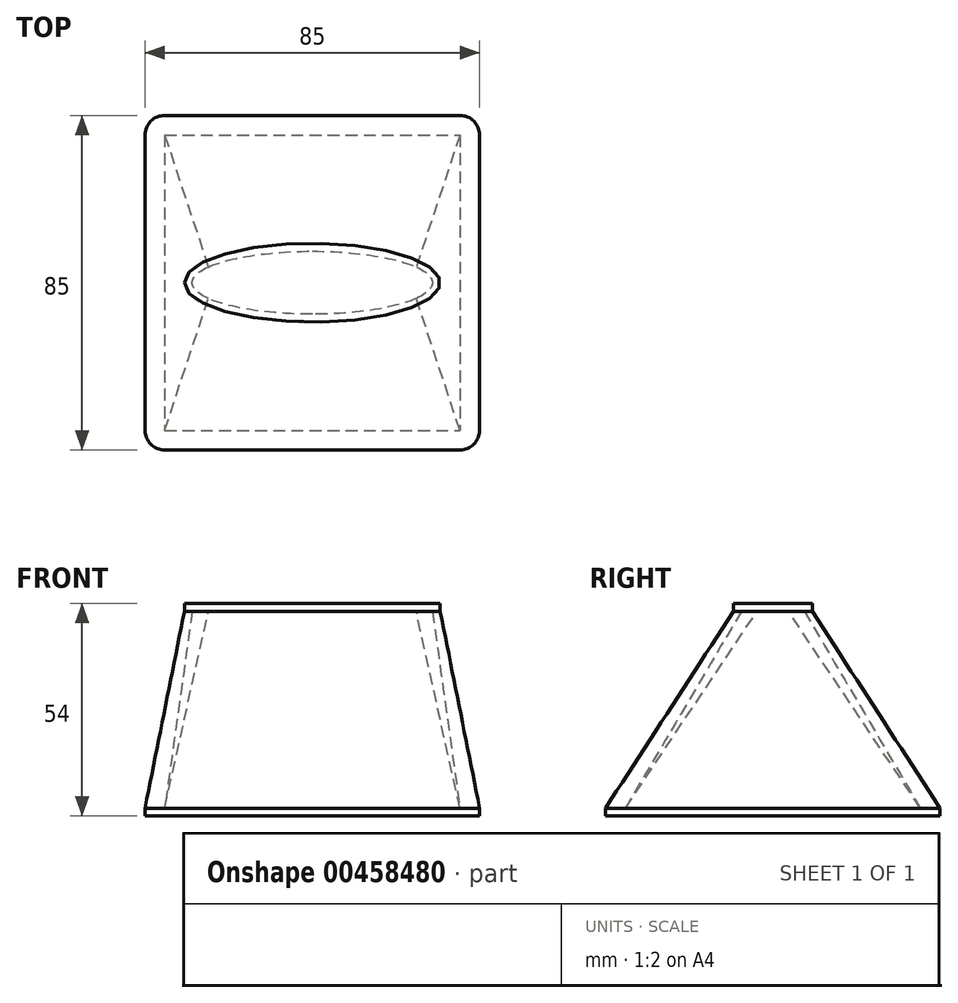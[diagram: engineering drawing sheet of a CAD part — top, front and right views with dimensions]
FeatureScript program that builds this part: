
annotation { "Feature Type Name" : "Feature", "Feature Type Description" : "" }
export const myFeature = defineFeature(function(context is Context, id is Id, definition is map)
    precondition{}
    {
        {
            var Q0;
            Q0=qCreatedBy(makeId("Top.planeOp"),FACE);
            var sketch = newSketch(context, id + "F0", { "sketchPlane" : qUnion([Q0])});
            skEllipse(sketch, "E0", {"center": v(0, 0) * mm, "majorRadius": 32.5 * mm, "minorRadius": 10 * mm, "majorAxis": v(-1, 0)});
            skSolve(sketch);
        }
        {
            var Q0;
            Q0=makeQuery(id+"F0.imprint","IMPRINT",FACE,{"disambiguationData":[TD([[makeQuery(id+"F0.imprint","IMPRINT",EDGE,{"derivedFrom":sQuery(id+"F0.wireOp",EDGE,"E0")}),1.0]])]});
            var Q1;
            Q1=sQuery(id+"F0.wireOp",EDGE,"E0");
            extrude(context, id + "F1", {"entities" : qUnion([Q0]), "surfaceEntities" : qUnion([Q1]), "depth" : 2 * mm});
        }
        {
            var Q0;
            Q0=makeQuery(id+"F1.opExtrude","SWEPT_BODY",BODY,{"disambiguationData":[OSD([sQuery(id+"F0.wireOp",EDGE,"E0")])]});
            transform(context, id + "F2", {"entities" : qUnion([Q0]), "transformType" : TransformType.TRANSLATION_3D, "dx" : 0 * mm, "dy" : 0 * mm, "dz" : 25 * mm, "makeCopy" : false});
        }
        {
            var Q0;
            Q0=qCreatedBy(makeId("Top.planeOp"),FACE);
            var sketch = newSketch(context, id + "F3", { "sketchPlane" : qUnion([Q0])});
            skLineSegment(sketch, "E1.bottom", {"start": v(-42.5, 42.5) * mm, "end": v(42.5, 42.5) * mm});
            skLineSegment(sketch, "E1.top", {"start": v(-42.5, -42.5) * mm, "end": v(42.5, -42.5) * mm});
            skLineSegment(sketch, "E1.left", {"start": v(-42.5, 42.5) * mm, "end": v(-42.5, -42.5) * mm});
            skLineSegment(sketch, "E1.right", {"start": v(42.5, 42.5) * mm, "end": v(42.5, -42.5) * mm});
            skLineSegment(sketch, "E2", {"start": v(0, -42.5) * mm, "end": v(0, 42.5) * mm, "construction": true});
            skSolve(sketch);
        }
        {
            var Q0;
            Q0 = qSketchRegion(id + "F3", true);
            extrude(context, id + "F4", {"entities" : qUnion([Q0]), "oppositeDirection" : true, "depth" : 2 * mm});
        }
        {
            var Q0;
            Q0=makeQuery(id+"F4.opExtrude","SWEPT_BODY",BODY,{"disambiguationData":[OSD([sQuery(id+"F3.wireOp",EDGE,"E1.bottom"),sQuery(id+"F3.wireOp",EDGE,"E1.top"),sQuery(id+"F3.wireOp",EDGE,"E1.left"),sQuery(id+"F3.wireOp",EDGE,"E1.right")])]});
            transform(context, id + "F5", {"entities" : qUnion([Q0]), "transformType" : TransformType.TRANSLATION_3D, "dx" : 0 * mm, "dy" : 0 * mm, "dz" : -25 * mm, "makeCopy" : false});
        }
        {
            var Q0;
            Q0=makeQuery(id+"Fj7gzEkDTdT3czc_2.opLoft","SWEPT_EDGE",EDGE,{"disambiguationData":[OSD([sQuery(id+"F0.wireOp",EDGE,"E0"),sQuery(id+"F3.wireOp",EDGE,"E1.bottom"),sQuery(id+"F3.wireOp",EDGE,"E1.left"),sQuery(id+"FQOJDwY7TzD2iMy_2.wireOp",EDGE,"0ff71cc1-0b0f-46e7-a495-bf6d35687e3b")])]});
            var Q1;
            Q1=makeQuery(id+"Fj7gzEkDTdT3czc_2.opLoft","SWEPT_EDGE",EDGE,{"disambiguationData":[OSD([sQuery(id+"F0.wireOp",EDGE,"E0"),sQuery(id+"F3.wireOp",EDGE,"E1.bottom"),sQuery(id+"F3.wireOp",EDGE,"E1.right"),sQuery(id+"FvGfQPQfCit8S9d_2.wireOp",EDGE,"579d9dbb-9344-4774-a39f-a0f3231496a0")])]});
            var Q2;
            Q2=makeQuery(id+"Fj7gzEkDTdT3czc_2.opLoft","SWEPT_EDGE",EDGE,{"disambiguationData":[OSD([sQuery(id+"F0.wireOp",EDGE,"E0"),sQuery(id+"F3.wireOp",EDGE,"E1.top"),sQuery(id+"F3.wireOp",EDGE,"E1.right"),sQuery(id+"FQOJDwY7TzD2iMy_2.wireOp",EDGE,"b4c446bf-a4a6-4e09-b549-f1406689d661")])]});
            var Q3;
            Q3=makeQuery(id+"Fj7gzEkDTdT3czc_2.opLoft","SWEPT_EDGE",EDGE,{"disambiguationData":[OSD([sQuery(id+"F0.wireOp",EDGE,"E0"),sQuery(id+"F3.wireOp",EDGE,"E1.top"),sQuery(id+"F3.wireOp",EDGE,"E1.left"),sQuery(id+"FvGfQPQfCit8S9d_2.wireOp",EDGE,"67149b96-056e-4209-8843-8e4786fcf0c8")])]});
            var Q4;
            Q4=makeQuery(id+"F4.opExtrude","SWEPT_EDGE",EDGE,{"disambiguationData":[OSD([sQuery(id+"F3.wireOp",EDGE,"E1.bottom"),sQuery(id+"F3.wireOp",EDGE,"E1.left")])]});
            var Q5;
            Q5=makeQuery(id+"F4.opExtrude","SWEPT_EDGE",EDGE,{"disambiguationData":[OSD([sQuery(id+"F3.wireOp",EDGE,"E1.bottom"),sQuery(id+"F3.wireOp",EDGE,"E1.right")])]});
            var Q6;
            Q6=makeQuery(id+"F4.opExtrude","SWEPT_EDGE",EDGE,{"disambiguationData":[OSD([sQuery(id+"F3.wireOp",EDGE,"E1.top"),sQuery(id+"F3.wireOp",EDGE,"E1.right")])]});
            var Q7;
            Q7=makeQuery(id+"F4.opExtrude","SWEPT_EDGE",EDGE,{"disambiguationData":[OSD([sQuery(id+"F3.wireOp",EDGE,"E1.top"),sQuery(id+"F3.wireOp",EDGE,"E1.left")])]});
            fillet(context, id + "F6", {"entities" : qUnion([Q0, Q1, Q2, Q3, Q4, Q5, Q6, Q7]), "radius" : 5 * mm, "tangentPropagation" : true, "allowEdgeOverflow" : false});
        }
        {
            var Q0;
            Q0=makeQuery(id+"F1.opExtrude","CAP_FACE",FACE,{"disambiguationData":[OSD([sQuery(id+"F0.wireOp",EDGE,"E0")])],"isStart":true});
            var sketch = newSketch(context, id + "F7", { "sketchPlane" : qUnion([Q0])});
            skEllipse(sketch, "E3", {"center": v(0, 0) * mm, "majorRadius": 30.5 * mm, "minorRadius": 8 * mm, "majorAxis": v(-1, 0)});
            skLineSegment(sketch, "E4", {"start": v(0, -8) * mm, "end": v(0, -10) * mm, "construction": true});
            skLineSegment(sketch, "E5", {"start": v(-30.5, 0) * mm, "end": v(-32.5, 0) * mm, "construction": true});
            skSolve(sketch);
        }
        {
            var Q0;
            Q0=makeQuery(id+"F4.opExtrude","CAP_FACE",FACE,{"disambiguationData":[OSD([sQuery(id+"F3.wireOp",EDGE,"E1.bottom"),sQuery(id+"F3.wireOp",EDGE,"E1.top"),sQuery(id+"F3.wireOp",EDGE,"E1.left"),sQuery(id+"F3.wireOp",EDGE,"E1.right")])],"isStart":true});
            var sketch = newSketch(context, id + "F8", { "sketchPlane" : qUnion([Q0])});
            skLineSegment(sketch, "E6.bottom", {"start": v(-37.5, 37.5) * mm, "end": v(37.5, 37.5) * mm});
            skLineSegment(sketch, "E6.top", {"start": v(-37.5, -37.5) * mm, "end": v(37.5, -37.5) * mm});
            skLineSegment(sketch, "E6.left", {"start": v(-37.5, 37.5) * mm, "end": v(-37.5, -37.5) * mm});
            skLineSegment(sketch, "E6.right", {"start": v(37.5, 37.5) * mm, "end": v(37.5, -37.5) * mm});
            skSolve(sketch);
        }
        {
            var Q0;
            Q0=qCreatedBy(makeId("Right.planeOp"),FACE);
            var sketch = newSketch(context, id + "F9", { "sketchPlane" : qUnion([Q0])});
            skLineSegment(sketch, "E7.0.0", {"start": v(42.5, -25) * mm, "end": v(37.5, -25) * mm});
            skLineSegment(sketch, "E7.0.1", {"start": v(37.5, -25) * mm, "end": v(-37.5, -25) * mm});
            skLineSegment(sketch, "E7.0.2", {"start": v(-37.5, -25) * mm, "end": v(-42.5, -25) * mm});
            skLineSegment(sketch, "E7.0.4", {"start": v(-42.5, -25) * mm, "end": v(-37.5, -25) * mm});
            skLineSegment(sketch, "E7.0.5", {"start": v(-37.5, -25) * mm, "end": v(37.5, -25) * mm});
            skLineSegment(sketch, "E7.0.6", {"start": v(37.5, -25) * mm, "end": v(42.5, -25) * mm});
            skLineSegment(sketch, "E8.0", {"start": v(10, 25) * mm, "end": v(-10, 25) * mm});
            skLineSegment(sketch, "E9.0", {"start": v(-8, 25) * mm, "end": v(8, 25) * mm});
            skFitSpline(sketch, "E10", {"points": [v(37.5, -25) * mm, v(8, 25) * mm], "startDerivative": vector(-29.5, 50) * mm, "endDerivative": vector(-29.5, 50) * mm});
            skFitSpline(sketch, "E11", {"points": [v(10, 25) * mm, v(42.5, -25) * mm], "startDerivative": vector(32.5, -50) * mm, "endDerivative": vector(32.5, -50) * mm});
            skFitSpline(sketch, "E12", {"points": [v(-37.5, -25) * mm, v(-8, 25) * mm], "startDerivative": vector(29.5, 50) * mm, "endDerivative": vector(29.5, 50) * mm});
            skFitSpline(sketch, "E13", {"points": [v(-10, 25) * mm, v(-42.5, -25) * mm], "startDerivative": vector(-32.5, -50) * mm, "endDerivative": vector(-32.5, -50) * mm});
            skSolve(sketch);
        }
        {
            var Q0;
            Q0=makeQuery(id+"F4.opExtrude","CAP_FACE",FACE,{"disambiguationData":[OSD([sQuery(id+"F3.wireOp",EDGE,"E1.bottom"),sQuery(id+"F3.wireOp",EDGE,"E1.top"),sQuery(id+"F3.wireOp",EDGE,"E1.left"),sQuery(id+"F3.wireOp",EDGE,"E1.right")])],"isStart":true});
            var Q1;
            Q1=makeQuery(id+"F1.opExtrude","CAP_FACE",FACE,{"disambiguationData":[OSD([sQuery(id+"F0.wireOp",EDGE,"E0")])],"isStart":true});
            var Q2;
            Q2=sQuery(id+"F9.wireOp",EDGE,"E11");
            var Q3;
            Q3=sQuery(id+"F9.wireOp",EDGE,"E13");
            loft(context, id + "F10", {"addGuides" : true, "sheetProfilesArray" : [{ "sheetProfileEntities" : qUnion([Q0]) }, { "sheetProfileEntities" : qUnion([Q1]) }], "guidesArray" : [{ "guideEntities" : qUnion([Q2]), "guideDerivativeType" : LoftGuideDerivativeType.DEFAULT, "guideDerivativeMagnitude" : 1 }, { "guideEntities" : qUnion([Q3]), "guideDerivativeType" : LoftGuideDerivativeType.DEFAULT, "guideDerivativeMagnitude" : 1 }]});
        }
        {
            var Q1;
            Q1=makeQuery(id+"F8.imprint","IMPRINT",FACE,{"disambiguationData":[TD([[makeQuery(id+"F8.imprint","IMPRINT",EDGE,{"derivedFrom":sQuery(id+"F8.wireOp",EDGE,"E6.bottom")}),-1.0]])]});
            var Q2;
            Q2=makeQuery(id+"F7.imprint","IMPRINT",FACE,{"disambiguationData":[TD([[makeQuery(id+"F7.imprint","IMPRINT",EDGE,{"derivedFrom":sQuery(id+"F7.wireOp",EDGE,"E3")}),1.0]])]});
            var Q3;
            Q3=sQuery(id+"F9.wireOp",EDGE,"E12");
            var Q4;
            Q4=sQuery(id+"F9.wireOp",EDGE,"E10");
            loft(context, id + "F11", {"operationType" : NewBodyOperationType.REMOVE, "addGuides" : true, "sheetProfilesArray" : [{ "sheetProfileEntities" : qUnion([Q1]) }, { "sheetProfileEntities" : qUnion([Q2]) }], "guidesArray" : [{ "guideEntities" : qUnion([Q3]), "guideDerivativeType" : LoftGuideDerivativeType.DEFAULT, "guideDerivativeMagnitude" : 1 }, { "guideEntities" : qUnion([Q4]), "guideDerivativeType" : LoftGuideDerivativeType.DEFAULT, "guideDerivativeMagnitude" : 1 }]});
        }
    });
